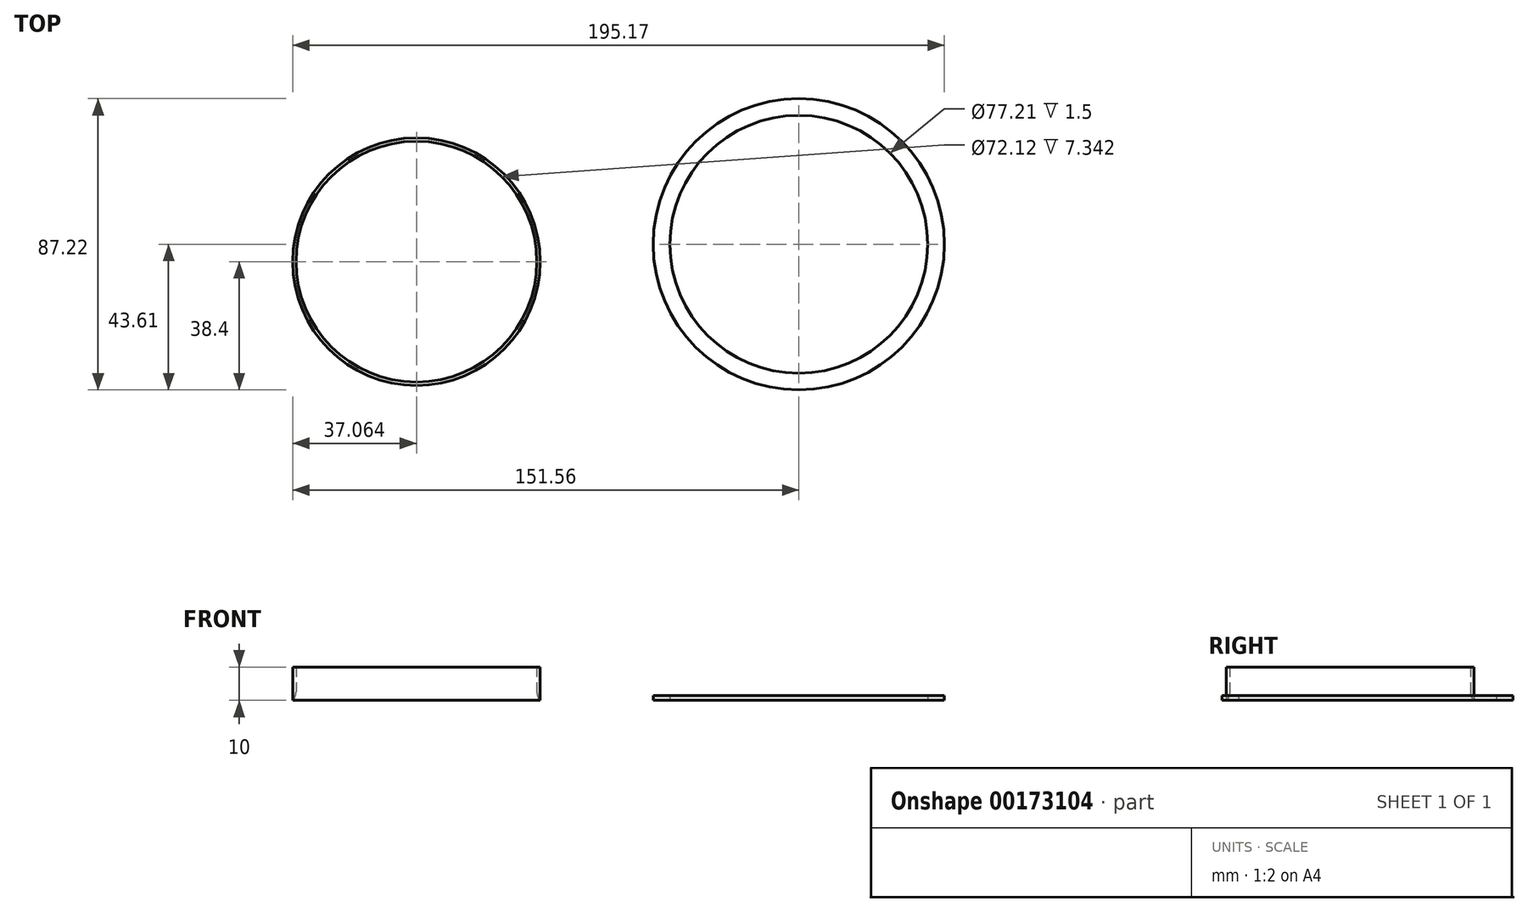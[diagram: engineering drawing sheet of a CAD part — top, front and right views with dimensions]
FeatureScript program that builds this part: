
annotation { "Feature Type Name" : "Feature", "Feature Type Description" : "" }
export const myFeature = defineFeature(function(context is Context, id is Id, definition is map)
    precondition{}
    {
        {
            var Q0;
            Q0=qCreatedBy(makeId("Top.planeOp"),FACE);
            var sketch = newSketch(context, id + "F0", { "sketchPlane" : qUnion([Q0])});
            skCircle(sketch, "E0", {"center": v(-114.5, -5.2) * mm, "radius": 36.06 * mm});
            skCircle(sketch, "E1.0", {"center": v(-114.5, -5.2) * mm, "radius": 38.06 * mm});
            skCircle(sketch, "E2", {"center": v(-114.5, -5.2) * mm, "radius": 37.07 * mm});
            skSolve(sketch);
        }
        {
            var Q0;
            Q0=qCreatedBy(makeId("Top.planeOp"),FACE);
            var sketch = newSketch(context, id + "F1", { "sketchPlane" : qUnion([Q0])});
            skCircle(sketch, "E3", {"center": v(0, 0) * mm, "radius": 38.6 * mm});
            skCircle(sketch, "E4.0", {"center": v(0, 0) * mm, "radius": 43.6 * mm});
            skSolve(sketch);
        }
        {
            var Q0;
            Q0=makeQuery(id+"F1.imprint","IMPRINT",FACE,{"disambiguationData":[TD([[makeQuery(id+"F1.imprint","IMPRINT",EDGE,{"derivedFrom":sQuery(id+"F1.wireOp",EDGE,"E3")}),-1.0]])]});
            extrude(context, id + "F2", {"entities" : qUnion([Q0]), "depth" : 1.5 * mm});
        }
        {
            var Q0;
            Q0 = qSketchRegion(id + "F4", true);
            var Q1;
            Q1=makeQuery(id+"F0.imprint","IMPRINT",FACE,{"disambiguationData":[TD([[makeQuery(id+"F0.imprint","IMPRINT",EDGE,{"derivedFrom":sQuery(id+"F0.wireOp",EDGE,"E0")}),-1.0]])]});
            extrude(context, id + "F3", {"entities" : qUnion([Q0, Q1]), "depth" : 10 * mm});
        }
        {
            var Q0;
            Q0=makeQuery(id+"F3.opExtrude","CAP_FACE",FACE,{"disambiguationData":[OSD([sQuery(id+"F0.wireOp",EDGE,"E0"),sQuery(id+"F0.wireOp",EDGE,"E1.0")])],"isStart":false});
            var sketch = newSketch(context, id + "F4", { "sketchPlane" : qUnion([Q0])});
            skCircle(sketch, "E5", {"center": v(-114.5, -5.2) * mm, "radius": 37 * mm});
            skSolve(sketch);
        }
        {
            var Q0;
            Q0=makeQuery(id+"F3.opExtrude","CAP_EDGE",EDGE,{"disambiguationData":[OSD([sQuery(id+"F0.wireOp",EDGE,"E0")])],"isStart":true});
            fillet(context, id + "F5", {"entities" : qUnion([Q0]), "radius" : 4 * mm, "tangentPropagation" : true, "allowEdgeOverflow" : false});
        }
    });
